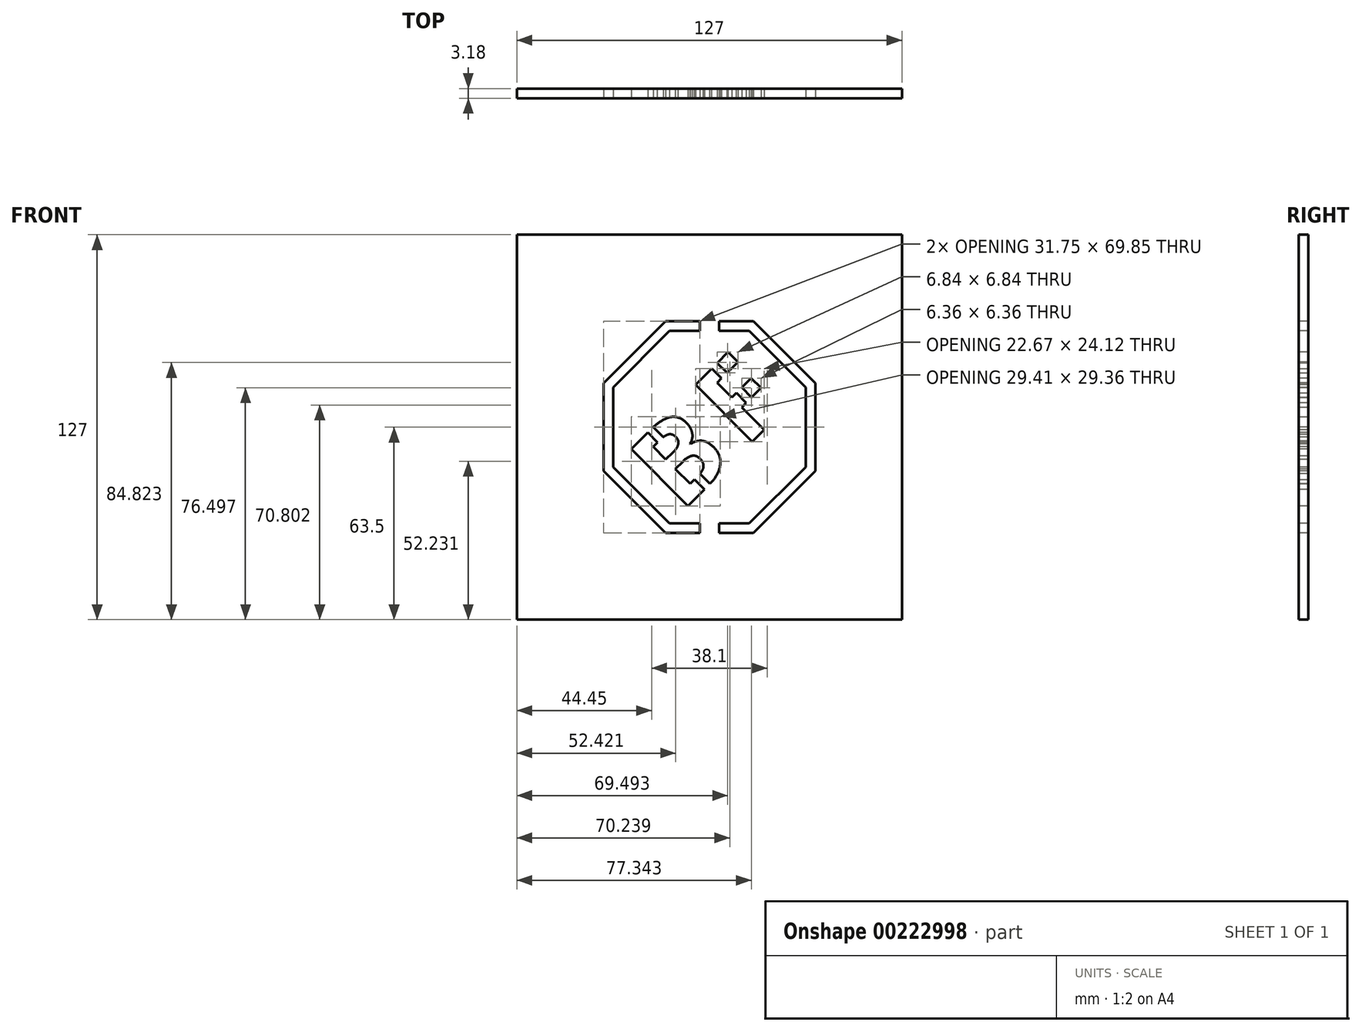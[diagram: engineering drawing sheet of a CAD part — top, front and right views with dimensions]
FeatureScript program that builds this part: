
annotation { "Feature Type Name" : "Feature", "Feature Type Description" : "" }
export const myFeature = defineFeature(function(context is Context, id is Id, definition is map)
    precondition{}
    {
        {
            var Q0;
            Q0=qCreatedBy(makeId("Front.planeOp"),FACE);
            var sketch = newSketch(context, id + "F0", { "sketchPlane" : qUnion([Q0])});
            skLineSegment(sketch, "E0.bottom", {"start": v(63.5, -63.5) * mm, "end": v(-63.5, -63.5) * mm});
            skLineSegment(sketch, "E0.top", {"start": v(63.5, 63.5) * mm, "end": v(-63.5, 63.5) * mm});
            skLineSegment(sketch, "E0.left", {"start": v(63.5, -63.5) * mm, "end": v(63.5, 63.5) * mm});
            skLineSegment(sketch, "E0.right", {"start": v(-63.5, -63.5) * mm, "end": v(-63.5, 63.5) * mm});
            skPoint(sketch, "E0.middle", {"position": v(0, 0) * mm});
            skSolve(sketch);
        }
        {
            var Q0;
            Q0 = qSketchRegion(id + "F0", true);
            extrude(context, id + "F1", {"entities" : qUnion([Q0]), "oppositeDirection" : true, "depth" : 3.17 * mm});
        }
        {
            var Q0;
            Q0=makeQuery(id+"F1.opExtrude","CAP_FACE",FACE,{"disambiguationData":[OSD([sQuery(id+"F0.wireOp",EDGE,"E0.bottom"),sQuery(id+"F0.wireOp",EDGE,"E0.top"),sQuery(id+"F0.wireOp",EDGE,"E0.left"),sQuery(id+"F0.wireOp",EDGE,"E0.right")])],"isStart":true});
            var sketch = newSketch(context, id + "F2", { "sketchPlane" : qUnion([Q0])});
            skCircle(sketch, "E1.cCircle", {"center": v(0, 0) * mm, "radius": 31.75 * mm, "construction": true});
            skLineSegment(sketch, "E1.0", {"start": v(13.15, -31.75) * mm, "end": v(3.17, -31.75) * mm});
            skLineSegment(sketch, "E1.1", {"start": v(-13.15, -31.75) * mm, "end": v(-31.75, -13.15) * mm});
            skLineSegment(sketch, "E1.2", {"start": v(-31.75, -13.15) * mm, "end": v(-31.75, 13.15) * mm});
            skLineSegment(sketch, "E1.3", {"start": v(-31.75, 13.15) * mm, "end": v(-13.15, 31.75) * mm});
            skLineSegment(sketch, "E1.4", {"start": v(-13.15, 31.75) * mm, "end": v(-3.17, 31.75) * mm});
            skLineSegment(sketch, "E1.5", {"start": v(13.15, 31.75) * mm, "end": v(31.75, 13.15) * mm});
            skLineSegment(sketch, "E1.6", {"start": v(31.75, 13.15) * mm, "end": v(31.75, -13.15) * mm});
            skLineSegment(sketch, "E1.7", {"start": v(31.75, -13.15) * mm, "end": v(13.15, -31.75) * mm});
            skPoint(sketch, "E1.0.midPoint", {"position": v(0, -31.75) * mm});
            skCircle(sketch, "E2.cCircle", {"center": v(0, 0) * mm, "radius": 34.93 * mm, "construction": true});
            skLineSegment(sketch, "E2.0", {"start": v(14.47, -34.93) * mm, "end": v(3.17, -34.93) * mm});
            skLineSegment(sketch, "E2.1", {"start": v(-14.47, -34.92) * mm, "end": v(-34.92, -14.47) * mm});
            skLineSegment(sketch, "E2.2", {"start": v(-34.92, -14.47) * mm, "end": v(-34.93, 14.47) * mm});
            skLineSegment(sketch, "E2.3", {"start": v(-34.92, 14.47) * mm, "end": v(-14.47, 34.92) * mm});
            skLineSegment(sketch, "E2.4", {"start": v(-14.47, 34.93) * mm, "end": v(-3.18, 34.93) * mm});
            skLineSegment(sketch, "E2.5", {"start": v(14.47, 34.93) * mm, "end": v(34.93, 14.47) * mm});
            skLineSegment(sketch, "E2.6", {"start": v(34.92, 14.47) * mm, "end": v(34.93, -14.47) * mm});
            skLineSegment(sketch, "E2.7", {"start": v(34.93, -14.47) * mm, "end": v(14.47, -34.93) * mm});
            skPoint(sketch, "E2.0.midPoint", {"position": v(0, -34.93) * mm});
            skLineSegment(sketch, "E3", {"start": v(0, 34.93) * mm, "end": v(0, 40.22) * mm});
            skPoint(sketch, "E3.endSnap0", {"position": v(0, 34.93) * mm});
            skLineSegment(sketch, "E4", {"start": v(-3.18, 34.93) * mm, "end": v(-3.18, 31.75) * mm});
            skLineSegment(sketch, "E5.MirrorCS", {"start": v(3.17, 34.93) * mm, "end": v(3.17, 31.75) * mm});
            skLineSegment(sketch, "E6.trimOffspring", {"start": v(-3.17, -31.75) * mm, "end": v(-3.17, -34.93) * mm});
            skLineSegment(sketch, "E7.trimOffspring", {"start": v(3.17, -31.75) * mm, "end": v(3.17, -34.93) * mm});
            skLineSegment(sketch, "E8.trimOffspring", {"start": v(3.17, 34.93) * mm, "end": v(14.47, 34.93) * mm});
            skLineSegment(sketch, "E9.trimOffspring", {"start": v(3.17, 31.75) * mm, "end": v(13.15, 31.75) * mm});
            skLineSegment(sketch, "E10.trimOffspring", {"start": v(-3.17, -31.75) * mm, "end": v(-13.15, -31.75) * mm});
            skLineSegment(sketch, "E11.trimOffspring", {"start": v(-3.17, -34.93) * mm, "end": v(-14.47, -34.93) * mm});
            skSolve(sketch);
        }
        {
            var Q0;
            Q0 = qSketchRegion(id + "F2", true);
            var Q1;
            Q1=makeQuery(id+"F1.opExtrude","CAP_FACE",FACE,{"disambiguationData":[OSD([sQuery(id+"F0.wireOp",EDGE,"E0.bottom"),sQuery(id+"F0.wireOp",EDGE,"E0.top"),sQuery(id+"F0.wireOp",EDGE,"E0.left"),sQuery(id+"F0.wireOp",EDGE,"E0.right")])],"isStart":false});
            extrude(context, id + "F3", {"entities" : qUnion([Q0]), "operationType" : NewBodyOperationType.REMOVE, "endBound" : BoundingType.UP_TO_SURFACE, "oppositeDirection" : true, "endBoundEntityFace" : qUnion([Q1]), "depth" : 25.4 * mm});
        }
        {
            var Q0;
            Q0=makeQuery(id+"F1.opExtrude","CAP_FACE",FACE,{"disambiguationData":[OSD([sQuery(id+"F0.wireOp",EDGE,"E0.bottom"),sQuery(id+"F0.wireOp",EDGE,"E0.top"),sQuery(id+"F0.wireOp",EDGE,"E0.left"),sQuery(id+"F0.wireOp",EDGE,"E0.right")])],"isStart":true});
            var sketch = newSketch(context, id + "F4", { "sketchPlane" : qUnion([Q0])});
            skText(sketch, "E12", { "text": "B", "fontName": "OpenSans-Bold.ttf"});
            skLineSegment(sketch, "E13", {"start": v(-0.9, -0.9) * mm, "end": v(0, 0) * mm, "construction": true});
            skText(sketch, "E14", { "text": "F", "fontName": "OpenSans-Bold.ttf"});
            skLineSegment(sketch, "E15", {"start": v(2.33, 2.33) * mm, "end": v(0, 0) * mm, "construction": true});
            const initialGuessF4  = {"E12": [-0.0094, -0.02831, 0.7071, 0.7071, 0.02673], "E14": [0.0118, -0.00712, 0.7071, 0.7071, 0.02675]};
            skSetInitialGuess(sketch, initialGuessF4);
            skSolve(sketch);
        }
        {
            var Q0;
            Q0 = qSketchRegion(id + "F4", true);
            var Q1;
            Q1=makeQuery(id+"F1.opExtrude","CAP_FACE",FACE,{"disambiguationData":[OSD([sQuery(id+"F0.wireOp",EDGE,"E0.bottom"),sQuery(id+"F0.wireOp",EDGE,"E0.top"),sQuery(id+"F0.wireOp",EDGE,"E0.left"),sQuery(id+"F0.wireOp",EDGE,"E0.right")])],"isStart":false});
            extrude(context, id + "F5", {"entities" : qUnion([Q0]), "operationType" : NewBodyOperationType.REMOVE, "endBound" : BoundingType.UP_TO_SURFACE, "oppositeDirection" : true, "endBoundEntityFace" : qUnion([Q1]), "depth" : 25.4 * mm});
        }
        {
            var Q0;
            {var subQ0=sQuery(id+"F0.wireOp",EDGE,"E0.bottom");var subQ1=sQuery(id+"F0.wireOp",EDGE,"E0.left");var subQ2=sQuery(id+"F0.wireOp",EDGE,"E0.top");var subQ3=sQuery(id+"F0.wireOp",EDGE,"E0.right");Q0=makeQuery(id+"F5.boolean.opBoolean","SPLIT",FACE,{"disambiguationData":[TD([makeQuery(id+"F1.opExtrude","SWEPT_FACE",FACE,{"disambiguationData":[OSD([subQ0])]})])],"derivedFrom":makeQuery(id+"F1.opExtrude","CAP_FACE",FACE,{"disambiguationData":[OSD([subQ0,subQ2,subQ1,subQ3])],"isStart":true})});}
            var sketch = newSketch(context, id + "F6", { "sketchPlane" : qUnion([Q0])});
            skLineSegment(sketch, "E16", {"start": v(-20.34, -1.76) * mm, "end": v(-13.73, -8.37) * mm});
            skLineSegment(sketch, "E17", {"start": v(-18.5, 0) * mm, "end": v(-11.93, -6.57) * mm});
            skLineSegment(sketch, "E18", {"start": v(-13.73, -8.37) * mm, "end": v(-11.93, -6.57) * mm});
            skLineSegment(sketch, "E19", {"start": v(-8.81, -13.29) * mm, "end": v(-7.02, -11.49) * mm});
            skLineSegment(sketch, "E20.trimOffspring", {"start": v(-8.81, -13.29) * mm, "end": v(-1.6, -20.5) * mm});
            skLineSegment(sketch, "E21.trimOffspring", {"start": v(-7.02, -11.49) * mm, "end": v(0.2, -18.7) * mm});
            skLineSegment(sketch, "E22", {"start": v(-20.34, -1.76) * mm, "end": v(-21.44, -0.66) * mm});
            skLineSegment(sketch, "E23", {"start": v(-21.44, -0.66) * mm, "end": v(-19.63, 1.15) * mm});
            skLineSegment(sketch, "E24", {"start": v(-19.63, 1.15) * mm, "end": v(-18.5, 0) * mm});
            skLineSegment(sketch, "E25", {"start": v(-1.6, -20.5) * mm, "end": v(-0.72, -21.38) * mm});
            skLineSegment(sketch, "E26", {"start": v(-0.72, -21.38) * mm, "end": v(1.56, -19.2) * mm});
            skLineSegment(sketch, "E27", {"start": v(1.56, -19.2) * mm, "end": v(0.2, -18.7) * mm});
            skLineSegment(sketch, "E28", {"start": v(0.77, 19.37) * mm, "end": v(13.47, 6.67) * mm});
            skLineSegment(sketch, "E29", {"start": v(13.47, 6.67) * mm, "end": v(15.27, 8.46) * mm});
            skLineSegment(sketch, "E30", {"start": v(15.27, 8.46) * mm, "end": v(2.57, 21.16) * mm});
            skLineSegment(sketch, "E31", {"start": v(2.57, 21.16) * mm, "end": v(0.77, 19.37) * mm});
            skSolve(sketch);
        }
        {
            var Q0;
            Q0 = qSketchRegion(id + "F6", true);
            var Q1;
            {var subQ0=sQuery(id+"F0.wireOp",EDGE,"E0.bottom");var subQ1=sQuery(id+"F0.wireOp",EDGE,"E0.left");var subQ2=sQuery(id+"F0.wireOp",EDGE,"E0.top");var subQ3=sQuery(id+"F0.wireOp",EDGE,"E0.right");Q1=makeQuery(id+"F5.boolean.opBoolean","SPLIT",FACE,{"disambiguationData":[TD([makeQuery(id+"F1.opExtrude","SWEPT_FACE",FACE,{"disambiguationData":[OSD([subQ0])]})])],"derivedFrom":makeQuery(id+"F1.opExtrude","CAP_FACE",FACE,{"disambiguationData":[OSD([subQ0,subQ2,subQ1,subQ3])],"isStart":false})});}
            extrude(context, id + "F7", {"entities" : qUnion([Q0]), "operationType" : NewBodyOperationType.ADD, "endBound" : BoundingType.UP_TO_SURFACE, "oppositeDirection" : true, "endBoundEntityFace" : qUnion([Q1]), "depth" : 25.4 * mm});
        }
    });
